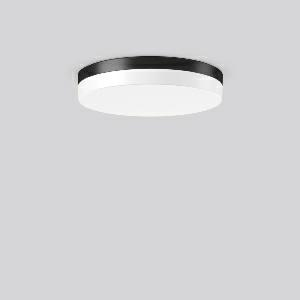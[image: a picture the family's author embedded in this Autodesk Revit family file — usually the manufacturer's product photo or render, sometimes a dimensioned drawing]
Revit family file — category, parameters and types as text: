
# Revit family: flat_slim_round_312632_0031_1_19_dd87
name_source: partatom
category: Lighting Fixtures
units: mm (PartAtom-declared; Revit-internal decimal feet)

## family parameters
Cut with Voids When Loaded = No
Host = Face
Light Source = No
Part Type = Normal
Room Calculation Point = No
Round Connector Dimension = Use Diameter
Shared = No

## types (1)
- MultiLumen 1 830 (1 x LED Modul 830, 2450 lm, 3000)
    Apparent Load = 18 VA
    CIE Flux Codes = 37 67 88 84 100
    Color Rendering = 80
    Color Temperature = 3000
    Default Elevation = 1800 mm
    Height = 70 mm
    Lamp = 1 x LED Modul 830
    Lamp Light Flux = 2450 lm
    Lamp count = 1
    Length = 400 mm
    Lifetime = 50000 h
    Luminous efficacy = 136 lm/W
    Manufacturer = RZB
    ModVariant = No
    Model = 312632.0031.1.19
    Mounting Place = Ceiling
    Mounting Type = Surface mounted
    Number of Poles = 1
    OnlyDefault = Yes
    Power Factor = 1
    Product Name = FLAT SLIM round
    Product group = Surface mounted ceiling and wall luminaires
    ProductGroupID = 305
    Protection Class = Protection class I
    Protection Degree = Degree of protection
    RLX_Detail_Level = 1
    RLX_Emergency_Light_Flux = 0 lm
    RLX_Emergency_Type = 0
    RLX_Emergency_Type_DB = No
    RlxData = <blob elided: 22173 chars, md5=f5e4a28a>
    Socket = socket
    Standby Power = 0 W
    System Light Flux = 2450 lm
    System Power = 18 W
    Type Comments = MultiLumen 1 830
    Type Image = 312631.0031.jpg
    URL = http://relux.com
    VarID = multilumen_1_830
    Voltage = 0 V
    Weight = 0.00 kg
    Width = 0 mm  [stored 0 ft]

note: [stored X ft] marks values corroborated as IEEE doubles in the binary element streams (Revit-internal decimal feet)

## geometry (parser evidence)
native form markers: Blend x4, Sweep x12
no freeform markers — native parametric forms only
